# Revit family: ERA_Клапан приточный_KP KIV
name_source: partatom
category: Оборудование
units: mm (PartAtom-declared; Revit-internal decimal feet)

## family parameters
Всегда вертикально = Да
Классификация = Нет
На основе рабочей плоскости = Нет
Общий = Нет
При загрузке вырезать с полостями = Нет
Размер круглого соединителя = Использовать диаметр
Тип детали = Вставляется
Точка расчета площади = Нет

## types (3) — shared parameters
ADSK_URL документации изделия = https://era.trade
ADSK_URL страницы изделия = https://era.trade
ADSK_Версия Revit = 2019
ADSK_Версия семейства = Ver.1 2025-02
ADSK_Единица измерения = шт.
ADSK_Завод-изготовитель = ООО «ЭРА»
ADSK_Количество = 1
ADSK_Размер_Высота = 190 мм
ADSK_Размер_Диаметр = 125 мм
ADSK_Размер_Ширина = 190 мм
ERA_Гарантия = 2 года
ERA_Количество в транспортной упаковке = 1
ERA_Контакты = 8 (4912) 70-16-76, 8 (4912) 24-16-00
ERA_Материал корпуса = пластик
ERA_Принцип вентиляции = Приточный
ERA_Размещение = в стену
ERA_Страна производитель = Россия
ERA_Торговая марка = ERA
ERA_Управление = Механическое
ERA_Цвет = Белый
ERA_Цвет (декоративный) = White
LT = ERA_Клапан приточный_KP KIV
URL = https://era.trade
Изготовитель = ООО «ЭРА»
Производитель_Контакты_Телефон = 8 (4912) 70-16-76, 8 (4912) 24-16-00

## per-type parameters (varying)
| type | ADSK_Материал | ADSK_Наименование | Code1 | ERA_Материал утеплителя |
| 12,5KP KIV050-01 | ERA_Условный_Белый | Клапан приточный 12,5KP KIV050-01 | 1 | мин.вата фольга |
| 12,5KP KIV050-02 | ERA_Пластик_Серебристый | Клапан приточный 12,5KP KIV050-02 | 2 | мин.вата |
| 12,5KP KIV050-03 | ERA_Пластик_Серебристый | Клапан приточный 12,5KP KIV050-03 | 3 | вспен.ПЭТ |

note: column(s) folded — value = type name in every type: ADSK_Код изделия, ADSK_Марка, ADSK_Обозначение
